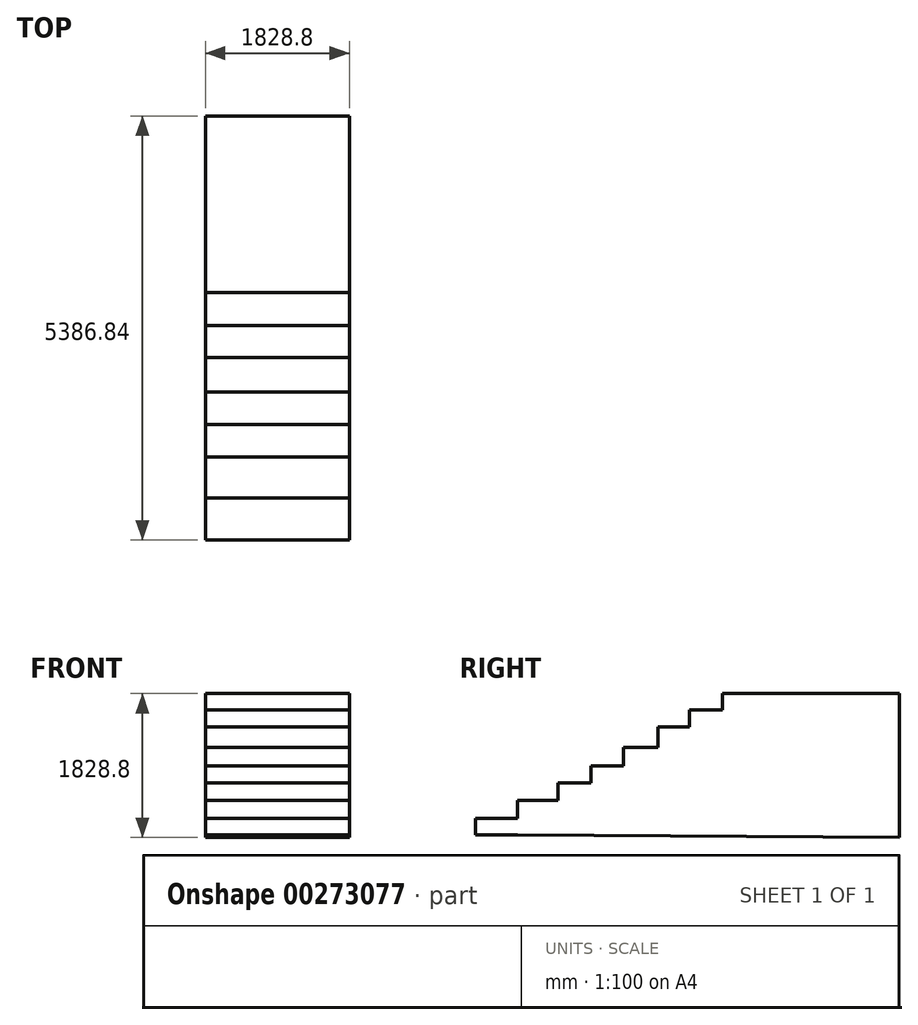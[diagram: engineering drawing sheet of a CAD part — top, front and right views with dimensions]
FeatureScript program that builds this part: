
annotation { "Feature Type Name" : "Feature", "Feature Type Description" : "" }
export const myFeature = defineFeature(function(context is Context, id is Id, definition is map)
    precondition{}
    {
        {
            var Q0;
            Q0=qCreatedBy(makeId("Right.planeOp"),FACE);
            var sketch = newSketch(context, id + "F0", { "sketchPlane" : qUnion([Q0])});
            skLineSegment(sketch, "E0", {"start": v(824.83, 920.46) * mm, "end": v(824.83, -908.34) * mm});
            skLineSegment(sketch, "E1", {"start": v(824.83, 920.46) * mm, "end": v(-1003.97, 920.46) * mm});
            skLineSegment(sketch, "E2.bottom", {"start": v(-1003.97, 920.46) * mm, "end": v(-1420.4, 920.46) * mm});
            skLineSegment(sketch, "E2.right", {"start": v(-1420.4, 920.46) * mm, "end": v(-1420.4, 710.5) * mm});
            skLineSegment(sketch, "E3.bottom", {"start": v(-1420.4, 710.5) * mm, "end": v(-1838.3, 710.5) * mm});
            skLineSegment(sketch, "E3.right", {"start": v(-1838.3, 710.5) * mm, "end": v(-1838.3, 499.09) * mm});
            skLineSegment(sketch, "E4.bottom", {"start": v(-1838.3, 499.09) * mm, "end": v(-2241.45, 499.09) * mm});
            skLineSegment(sketch, "E4.right", {"start": v(-2241.45, 499.09) * mm, "end": v(-2241.45, 238.52) * mm});
            skLineSegment(sketch, "E5.bottom", {"start": v(-2241.45, 238.52) * mm, "end": v(-2679, 238.52) * mm});
            skLineSegment(sketch, "E5.right", {"start": v(-2679, 238.52) * mm, "end": v(-2679, 0) * mm});
            skLineSegment(sketch, "E6.bottom", {"start": v(-2679, 0) * mm, "end": v(-3092, 0) * mm});
            skLineSegment(sketch, "E6.right", {"start": v(-3092, 0) * mm, "end": v(-3092, -213.8) * mm});
            skLineSegment(sketch, "E7.bottom", {"start": v(-3092, -213.8) * mm, "end": v(-3509.89, -213.8) * mm});
            skLineSegment(sketch, "E7.right", {"start": v(-3509.89, -213.8) * mm, "end": v(-3509.89, -435.04) * mm});
            skLineSegment(sketch, "E8.bottom", {"start": v(-3509.89, -435.04) * mm, "end": v(-4026.11, -435.04) * mm});
            skLineSegment(sketch, "E8.right", {"start": v(-4026.11, -435.04) * mm, "end": v(-4026.11, -666.1) * mm});
            skLineSegment(sketch, "E9.bottom", {"start": v(-4026.11, -666.1) * mm, "end": v(-4562, -666.1) * mm});
            skLineSegment(sketch, "E9.top", {"start": v(-4026.11, -877.52) * mm, "end": v(-4562, -877.52) * mm});
            skLineSegment(sketch, "E9.right", {"start": v(-4562, -666.1) * mm, "end": v(-4562, -877.52) * mm});
            skLineSegment(sketch, "E10", {"start": v(-4026.11, -877.52) * mm, "end": v(824.83, -908.34) * mm});
            skSolve(sketch);
        }
        {
            var Q0;
            Q0 = qSketchRegion(id + "F0", true);
            extrude(context, id + "F1", {"entities" : qUnion([Q0]), "depth" : 1828.8 * mm});
        }
    });
